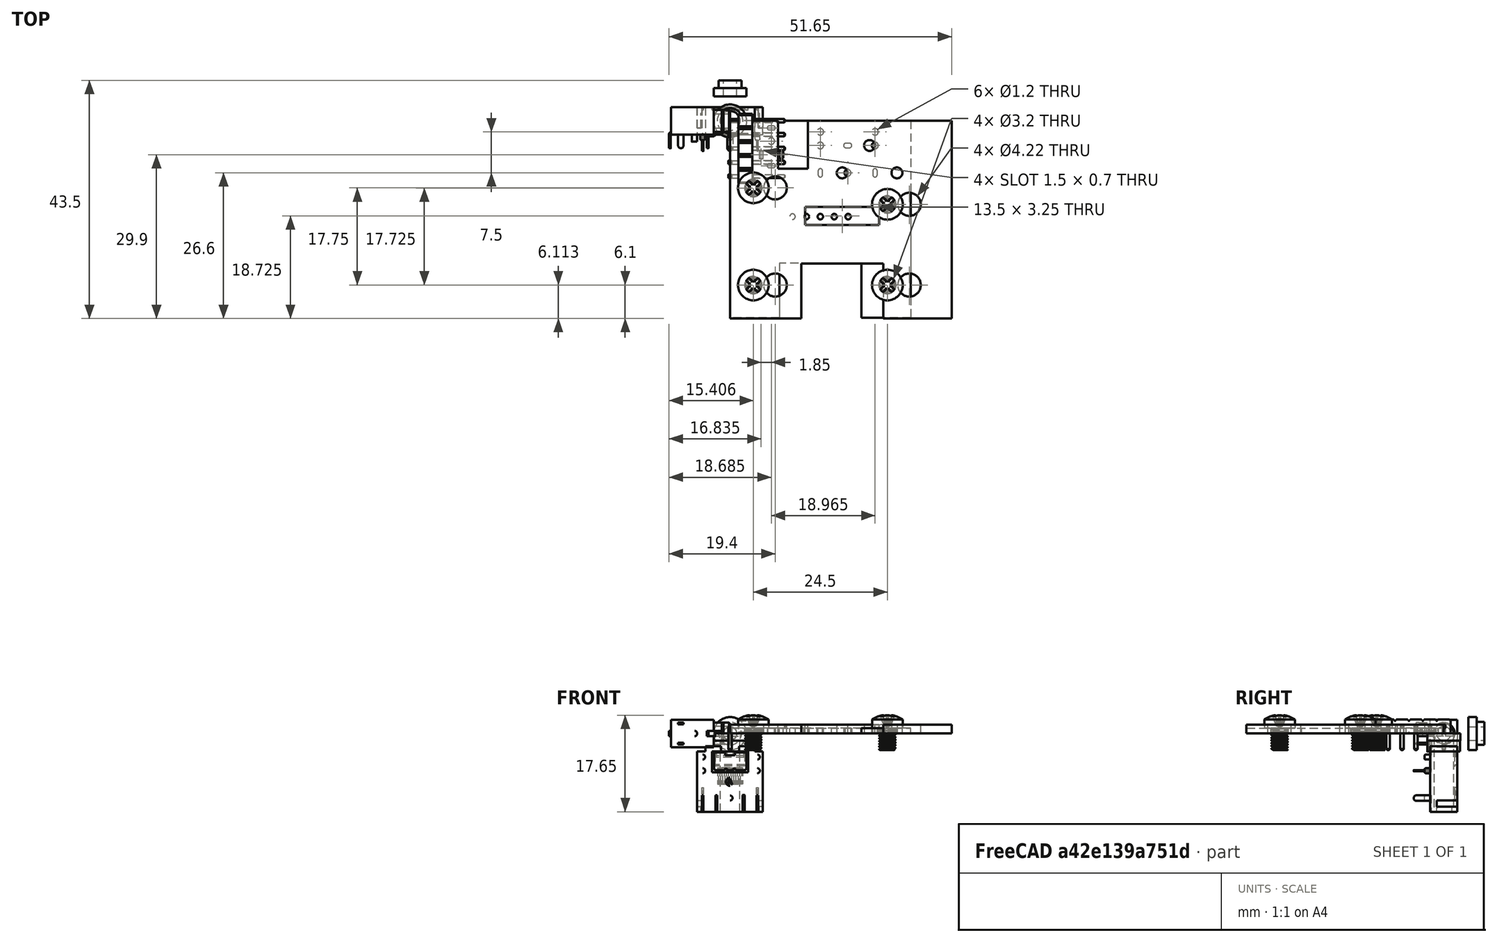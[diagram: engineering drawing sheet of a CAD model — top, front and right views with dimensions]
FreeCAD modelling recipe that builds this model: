
FCSTD DOCUMENT  (FreeCAD 0.20R)
Label: SH101_IO_MOD_GRIP_BOARD
License: All rights reserved
LicenseURL: http://en.wikipedia.org/wiki/All_rights_reserved
objects: Part::Feature×9, App::Part×9, Part::FeaturePython×4
note: 13 computed .brp shape members not serialized (recipe doc carries the construction recipe); baked Part::Feature solids carry a one-line shape summary decoded from their .brp

FEATURE [Part::Feature] Part__Feature  label="SOLID"
  shape: bbox 12 x 8.748 x 14.3 mm, 251 faces (baked)
FEATURE [App::Part] CUI_DEVICES_SJ1_3523N  label="CUI_DEVICES_SJ1-3523N"
  Group = -> [Part__Feature]
  Origin = -> Origin
  Placement = pos=(21.5,2.3,3.55) rot=(0,0.707107,0.707107;3.14159rad)
FEATURE [Part::Feature] Part__Feature001  label="COMPOUND"
  shape: bbox 11.15 x 7.5 x 5 mm, 68 faces, 4 solids (baked)
FEATURE [App::Part] CUI_DEVICES_SJ1_2503A  label="CUI_DEVICES_SJ1-2503A"
  Group = -> [Part__Feature001]
  Origin = -> Origin001
  Placement = pos=(7.5347,2.8,3.55) rot=(0.57735,0.57735,0.57735;2.0944rad)
FEATURE [Part::Feature] Part__Feature002  label="SOLID001"
  shape: bbox 10.36 x 12.7 x 5.54 mm, 139 faces (baked)
FEATURE [App::Part] PinHeader_1x05_P2_54mm_Horizontal  label="PinHeader_1x05_P2.54mm_Horizontal"
  Group = -> [Part__Feature002]
  Origin = -> Origin002
  Placement = pos=(21.575,-17.5,1.05) rot=(0,0,-1;1.5708rad)
FEATURE [Part::Feature] Part__Feature003  label="SH101_IO PCB"
  shape: bbox 33 x 36 x 1 mm, 53 faces (baked)
FEATURE [App::Part] SH101_IO_1  label="SH101_IO 1"
  Group = -> [CUI_DEVICES_SJ1_3523N,CUI_DEVICES_SJ1_2503A,PinHeader_1x05_P2_54mm_Horizontal,Part__Feature003]
  Origin = -> Origin003
  Placement = pos=(0,0,0.1) rot=(0,0,1;0rad)
FEATURE [Part::Feature] Part__Feature004  label="SOLID002"
  shape: bbox 10.39 x 2.9 x 9 mm, 6 faces (baked)
FEATURE [App::Part] SMTSO3015CTJ
  Group = -> [Part__Feature004]
  Origin = -> Origin004
  Placement = pos=(8.25,-30,7.65) rot=(-1,0,0;1.5708rad)
FEATURE [Part::Feature] Part__Feature005  label="SOLID003"
  shape: bbox 10.39 x 2.9 x 9 mm, 6 faces (baked)
FEATURE [App::Part] SMTSO3015CTJ001
  Group = -> [Part__Feature005]
  Origin = -> Origin005
  Placement = pos=(8.25,-12.25,7.65) rot=(-1,0,0;1.5708rad)
FEATURE [Part::Feature] Part__Feature006  label="SOLID004"
  shape: bbox 10.39 x 2.9 x 9 mm, 6 faces (baked)
FEATURE [App::Part] SMTSO3015CTJ002
  Group = -> [Part__Feature006]
  Origin = -> Origin006
  Placement = pos=(32.75,-30,7.65) rot=(-1,0,0;1.5708rad)
FEATURE [Part::Feature] Part__Feature007  label="SOLID005"
  shape: bbox 10.39 x 2.9 x 9 mm, 6 faces (baked)
FEATURE [App::Part] SMTSO3015CTJ003
  Group = -> [Part__Feature007]
  Origin = -> Origin007
  Placement = pos=(32.75,-15.25,7.65) rot=(-1,0,0;1.5708rad)
FEATURE [Part::Feature] Part__Feature008  label="SH101_MOD_GRIP_BOARD PCB"
  shape: bbox 40.5 x 36.1 x 1.6 mm, 25 faces (baked)
FEATURE [App::Part] SH101_MOD_GRIP_BOARD_1  label="SH101_MOD_GRIP_BOARD 1"
  Group = -> [SMTSO3015CTJ,SMTSO3015CTJ001,SMTSO3015CTJ002,SMTSO3015CTJ003,Part__Feature008]
  Origin = -> Origin008
  Placement = pos=(-4,0,-3) rot=(0,0,1;0rad)
FEATURE [Part::FeaturePython] Screw  label="M3x4-Screw"  # Fasteners workbench fastener (typed FeaturePython)
  Placement = pos=(4.25,-12.25,1) rot=(0,0,1;0rad)
  diameter = 4
  invert = false
  leftHanded = false
  length = 11
  lengthCustom = 4
  matchOuter = false
  offset = 0
  thread = true
  type = 49
FEATURE [Part::FeaturePython] Screw001  label="M3x4-Screw007"  # Fasteners workbench fastener (typed FeaturePython)
  Placement = pos=(4.25,-30,1) rot=(0,0,1;0rad)
  diameter = 4
  invert = false
  leftHanded = false
  length = 11
  lengthCustom = 4
  matchOuter = false
  offset = 0
  thread = true
  type = 49
FEATURE [Part::FeaturePython] Screw002  label="M3x4-Screw005"  # Fasteners workbench fastener (typed FeaturePython)
  Placement = pos=(28.75,-30,1) rot=(0,0,1;0rad)
  diameter = 4
  invert = false
  leftHanded = false
  length = 11
  lengthCustom = 4
  matchOuter = false
  offset = 0
  thread = true
  type = 49
FEATURE [Part::FeaturePython] Screw003  label="M3x4-Screw006"  # Fasteners workbench fastener (typed FeaturePython)
  Placement = pos=(28.75,-15.25,1) rot=(0,0,1;0rad)
  diameter = 4
  invert = false
  leftHanded = false
  length = 11
  lengthCustom = 4
  matchOuter = false
  offset = 0
  thread = true
  type = 49
